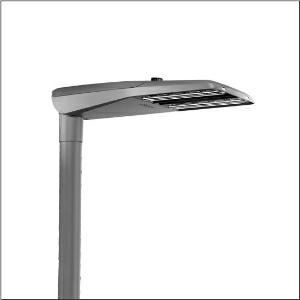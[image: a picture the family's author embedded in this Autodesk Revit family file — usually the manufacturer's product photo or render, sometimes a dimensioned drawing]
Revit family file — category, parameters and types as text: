
# Revit family: streetlight_sl_11_iq_midi___st1_2a_5xc3a41u08le_6743
name_source: partatom
category: Lighting Fixtures
units: mm (PartAtom-declared; Revit-internal decimal feet)

## family parameters
Cut with Voids When Loaded = No
Host = Face
Light Source = No
Part Type = Normal
Room Calculation Point = No
Round Connector Dimension = Use Diameter
Shared = No

## types (1)
- --- (1 x LED, 9590 lm, 59.4 W, 4000K)
    Apparent Load = 59 VA
    CIE Flux Codes = 32 70 96 100 100
    Color Rendering = 70
    Color Temperature = 4000K
    Default Elevation = 1800 mm
    Description = Streetlight SL 11 iQ midi, mast luminaire, primary light control with 3 zone facetted reflector, of plastic, silver coated, highly specular, primary optical cover: cover, of PMMA, transparent, light distribution: ST1.2a, light emission: direct distribution, primary light characteristic: asymmetric, installation type: post-top, side-entry, LED, High Power LED, rated luminous flux: 9.590lm, luminous efficacy: 161lm/W, light colour: 740, colour temperature: 4000K, control: presetting dimming logarithmic, Street-Remote, Auto-Match, Temp-Guard, Lumen-Switch, Night-Set, Smart-Wire, Light-Fading, Desk-Remote (wireless, voltage-free reading and setting of iQ features in the workshop via application-optimized NFC function/RFID function), optimised constant luminous flux control (CLO 2.0), with cable H07RN-F 5x 1.5mm², mains connection: 230..240V, AC, 50/60Hz, connection cable pre-assembled, cable length: 8,5m, start of lifetime: 59W, end of service life: 62W, reduction: 29W, luminaire housing, of diecast aluminium, powder-coated, Siteco® metallic grey (DB 702S), please order mast flange separately, inclination adjustable without tools: 0°, 5°, 10°, 15° (post-top) | 0°, -5°, -10°, -15° (side-entry), sealing non-destructively replaceable, multi-level sealing system, length: 780mm, width: 376mm, height: 118mm, mast flange for spigot size: 42mm (side-entry): 5XC10008XM4, 60/48mm (side-entry/post-top): 5XC10108XM2, 76/60mm (side-entry/post-top): 5XC10108XM1, equipment: standard, Smart Interface below, protection rating (complete): IP66, insulation class (complete): insulation class II (safety insulation), certification: CE, ENEC, VDE, UKCA, impact resistance: IK09, permissible operating ambient temperature for outdoor applications: -25..+50°C, standard-compliant lighting for roads and squares, Environmental Product Declaration (EPD) tested and certified by an independent institute, packaging unit: 1 piece

Light Distribution: ST1.2a
    Height = 118 mm
    Lamp = 1 x LED
    Lamp Light Flux = 9590 lm
    Lamp Power = 59.4 W
    Lamp count = 1
    Length = 780 mm
    Luminous efficacy = 161 lm/W
    Manufacturer = Siteco
    ModVariant = No
    Model = 5XC3A41U08LE
    Number of Poles = 1
    OnlyDefault = Yes
    Power Factor = 1
    Product Name = Streetlight SL 11 iQ midi | ST1.2a
    Product group = mast luminaire | pylon top
    ProductGroupID = 6100
    Protection Class = Protection class II
    Protection Degree = IP 66
    RLX_Detail_Level = 1
    RLX_Emergency_Light_Flux = 0 lm
    RLX_Emergency_Type = 0
    RLX_Emergency_Type_DB = No
    RlxData = <blob elided: 69629 chars, md5=ae7dc15f>
    Socket = socket
    Standby Power = 0 W
    System Light Flux = 9590 lm
    System Power = 59 W
    Type Comments = factory setting: luminous flux: 100 % | dim-lin: 254 | 521 mA
    Type Image = l_1005968.jpg
    URL = http://relux.com
    VarID = @adj_082491
    Voltage = 0 V
    Weight = 0.00 kg
    Width = 376 mm

## geometry (parser evidence)
native form markers: Blend x4, Sweep x9
no freeform markers — native parametric forms only
